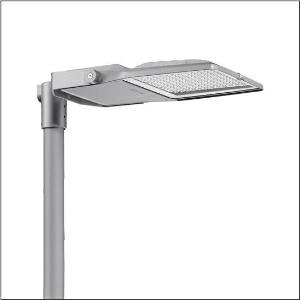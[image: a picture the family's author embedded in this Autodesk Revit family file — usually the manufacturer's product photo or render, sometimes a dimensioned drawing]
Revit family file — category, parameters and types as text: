
# Revit family: floodlight_fl_21_midi___pl61_5xa7786e2c3a_519c
name_source: partatom
category: Lighting Fixtures
units: mm (PartAtom-declared; Revit-internal decimal feet)

## family parameters
Cut with Voids When Loaded = No
Host = Face
Light Source = No
Part Type = Normal
Room Calculation Point = No
Round Connector Dimension = Use Diameter
Shared = No

## types (1)
- --- (1 x LED, 26450 lm, 212.4 W, 3000K)
    Apparent Load = 212 VA
    CIE Flux Codes = 33 65 98 100 100
    Color Rendering = 70
    Color Temperature = 3000K
    Default Elevation = 1800 mm
    Description = Floodlight FL 21 midi, floodlight, primary light control with lens, of PMMA, primary optical cover: protective disc, of toughened safety glass, transparent, light distribution: PL61, light emission: direct distribution, installation type: surface-mounted, LED, High Power LED, rated luminous flux: 26.450lm, luminous efficacy: 125lm/W, light colour: 730, colour temperature: 3000K, control gear: ECG Smart Interface, control: flexible luminous flux parameterisation, time-dependent luminous flux control, constant luminous flux control, overheat protection, pre-setting: logarithmic dimming characteristic, with terminal, 6-pole, mains connection: 220..240V, AC, 50/60Hz, start of lifetime: 212W, end of service life: 231W, reduction: 95W, luminaire housing, of diecast aluminium, powder-coated, Siteco® metallic grey (DB 702S), corrosivity category C5 mid according to DIN EN ISO 12944, sealing non-destructively replaceable, please order mast flange separately, mast bracket, of steel, galvanised, powder-coated, Siteco® metallic grey (DB 702S), Smart Interface below and above, protection rating (complete): IP66, insulation class (complete): insulation class II (safety insulation), certification: CE, ENEC, VDE, protection symbol: D, impact resistance: IK08, permissible operating ambient temperature: -40..+40°C, permissible operating ambient temperature for outdoor applications: -40..+50°C, standard: DIN EN 12944, LABS conformity tested according to VDMA 24364:2018-05, packaging unit: 1 piece

Light Distribution: PL61
    Height = 76 mm
    Lamp = 1 x LED
    Lamp Light Flux = 26450 lm
    Lamp Power = 212.4 W
    Lamp count = 1
    Length = 657 mm
    Luminous efficacy = 125 lm/W
    Manufacturer = Siteco
    ModVariant = No
    Model = 5XA7786E2C3A
    Number of Poles = 1
    OnlyDefault = Yes
    Power Factor = 1
    Product Name = Floodlight FL 21 midi | PL61
    Product group = floodlight | pylon annexe
    ProductGroupID = 6200
    Protection Class = Protection class II
    Protection Degree = IP 66
    RLX_Detail_Level = 1
    RLX_Emergency_Light_Flux = 0 lm
    RLX_Emergency_Type = 0
    RLX_Emergency_Type_DB = No
    RlxData = <blob elided: 153701 chars, md5=08c13b86>
    Socket = socket
    Standby Power = 0 W
    System Light Flux = 26450 lm
    System Power = 212 W
    Type Comments = factory setting: luminous flux: 100 % | dim-lin: 254 | 710 mA
    Type Image = l_1007123.jpg
    URL = http://relux.com
    VarID = @adj_166761
    Voltage = 0 V
    Weight = 0.00 kg
    Width = 442 mm

## geometry (parser evidence)
native form markers: Blend x4, Sweep x16
no freeform markers — native parametric forms only
